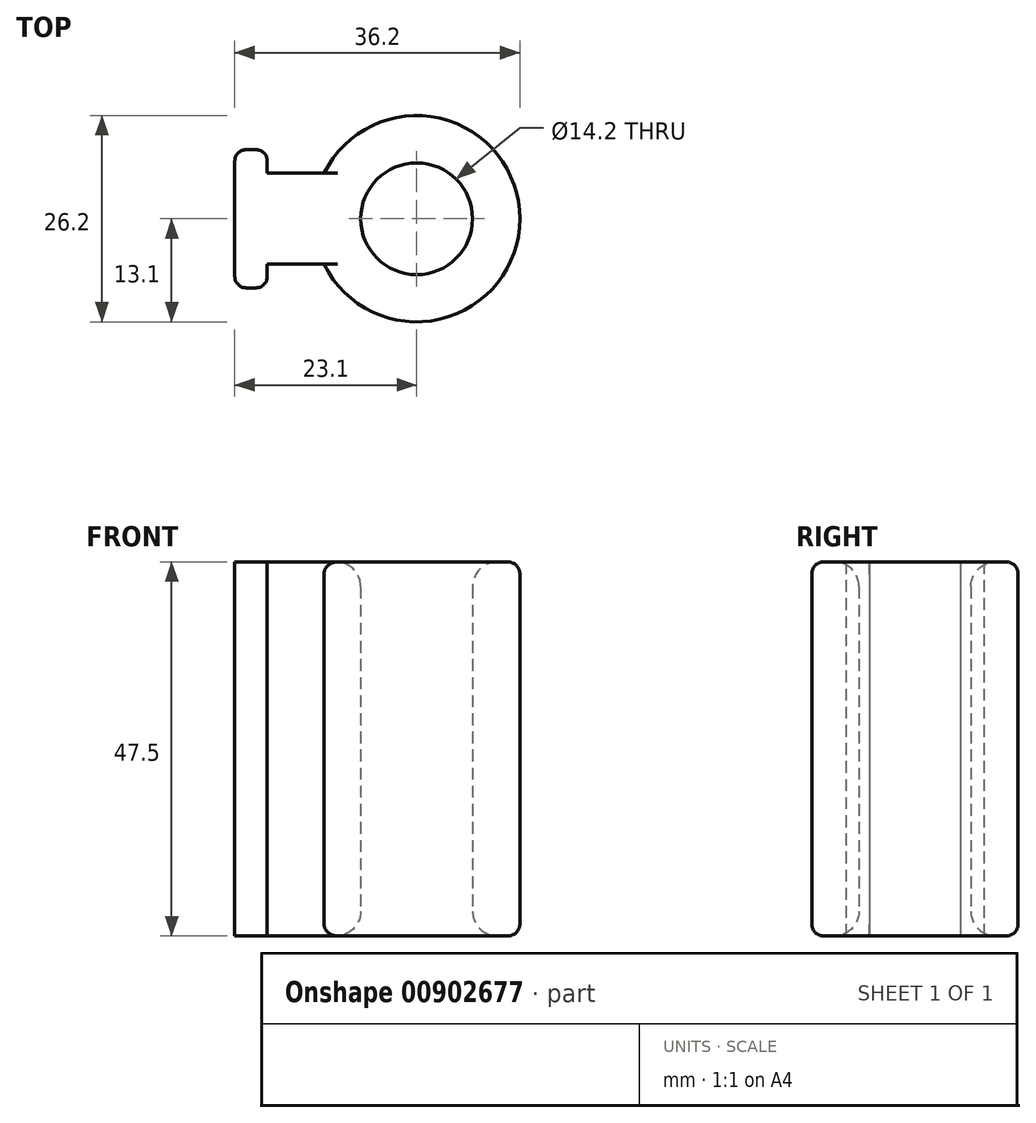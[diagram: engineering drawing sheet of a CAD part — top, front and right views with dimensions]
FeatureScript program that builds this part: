
annotation { "Feature Type Name" : "Feature", "Feature Type Description" : "" }
export const myFeature = defineFeature(function(context is Context, id is Id, definition is map)
    precondition{}
    {
        {
            var Q0;
            Q0=qCreatedBy(makeId("Top.planeOp"),FACE);
            var sketch = newSketch(context, id + "F0", { "sketchPlane" : qUnion([Q0])});
            skCircle(sketch, "E0", {"center": v(0, 0) * mm, "radius": 7.1 * mm});
            skCircle(sketch, "E1", {"center": v(0, 0) * mm, "radius": 13.1 * mm});
            skLineSegment(sketch, "E2.bottom", {"start": v(-11.76, 5.78) * mm, "end": v(-23.1, 5.78) * mm});
            skLineSegment(sketch, "E2.top", {"start": v(-11.76, -5.78) * mm, "end": v(-23.1, -5.78) * mm});
            skLineSegment(sketch, "E2.left", {"start": v(-11.76, 5.78) * mm, "end": v(-11.76, -5.78) * mm});
            skLineSegment(sketch, "E2.right", {"start": v(-23.1, 5.78) * mm, "end": v(-23.1, -5.78) * mm});
            skLineSegment(sketch, "E3.bottom", {"start": v(-23.1, 8.78) * mm, "end": v(-18.97, 8.78) * mm});
            skLineSegment(sketch, "E3.top", {"start": v(-23.1, -8.78) * mm, "end": v(-18.97, -8.78) * mm});
            skLineSegment(sketch, "E3.left", {"start": v(-23.1, 8.78) * mm, "end": v(-23.1, -8.78) * mm});
            skLineSegment(sketch, "E3.right", {"start": v(-18.97, 8.78) * mm, "end": v(-18.97, -8.78) * mm});
            skSolve(sketch);
        }
        {
            var Q0;
            Q0=makeQuery(id+"F0.imprint","IMPRINT",FACE,{"disambiguationData":[TD([[makeQuery(id+"F0.imprint","IMPRINT",EDGE,{"derivedFrom":sQuery(id+"F0.wireOp",EDGE,"E0")}),-1.0]])]});
            var Q1;
            {var subQ1=sQuery(id+"F0.wireOp",EDGE,"E2.bottom");Q1=makeQuery(id+"F0.imprint","IMPRINT",FACE,{"disambiguationData":[TD([[makeQuery(id+"F0.imprint","IMPRINT",EDGE,{"derivedFrom":subQ1}),1.0]])]});}
            var Q2;
            {var subQ0=sQuery(id+"F0.wireOp",EDGE,"E2.left");Q2=makeQuery(id+"F0.imprint","IMPRINT",FACE,{"disambiguationData":[TD([[makeQuery(id+"F0.imprint","IMPRINT",EDGE,{"derivedFrom":subQ0}),-1.0]])]});}
            var Q3;
            {var subQ5=sQuery(id+"F0.wireOp",EDGE,"E3.bottom");Q3=makeQuery(id+"F0.imprint","IMPRINT",FACE,{"disambiguationData":[TD([[makeQuery(id+"F0.imprint","IMPRINT",EDGE,{"derivedFrom":subQ5}),-1.0]])]});}
            var Q4;
            {var subQ5=sQuery(id+"F0.wireOp",EDGE,"E3.top");Q4=makeQuery(id+"F0.imprint","IMPRINT",FACE,{"disambiguationData":[TD([[makeQuery(id+"F0.imprint","IMPRINT",EDGE,{"derivedFrom":subQ5}),1.0]])]});}
            extrude(context, id + "F1", {"entities" : qUnion([Q0, Q1, Q2, Q3, Q4]), "depth" : 47.5 * mm, "offsetDistance" : 25 * mm});
        }
        {
            var Q0;
            Q0=makeQuery(id+"F1.opExtrude","SWEPT_EDGE",EDGE,{"disambiguationData":[OSD([sQuery(id+"F0.wireOp",EDGE,"E3.top"),sQuery(id+"F0.wireOp",EDGE,"E3.left")])]});
            var Q1;
            Q1=makeQuery(id+"F1.opExtrude","SWEPT_EDGE",EDGE,{"disambiguationData":[OSD([sQuery(id+"F0.wireOp",EDGE,"E3.bottom"),sQuery(id+"F0.wireOp",EDGE,"E3.left")])]});
            var Q2;
            Q2=makeQuery(id+"F1.opExtrude","SWEPT_EDGE",EDGE,{"disambiguationData":[OSD([sQuery(id+"F0.wireOp",EDGE,"E3.top"),sQuery(id+"F0.wireOp",EDGE,"E3.right")])]});
            var Q3;
            Q3=makeQuery(id+"F1.opExtrude","SWEPT_EDGE",EDGE,{"disambiguationData":[OSD([sQuery(id+"F0.wireOp",EDGE,"E3.bottom"),sQuery(id+"F0.wireOp",EDGE,"E3.right")])]});
            fillet(context, id + "F2", {"entities" : qUnion([Q0, Q1, Q2, Q3]), "radius" : 1.45 * mm, "tangentPropagation" : true, "allowEdgeOverflow" : false});
        }
        {
            var Q0;
            Q0=makeQuery(id+"F1.opExtrude","CAP_EDGE",EDGE,{"disambiguationData":[OSD([sQuery(id+"F0.wireOp",EDGE,"E0")])],"isStart":false});
            var Q1;
            Q1=makeQuery(id+"F1.opExtrude","CAP_EDGE",EDGE,{"disambiguationData":[OSD([sQuery(id+"F0.wireOp",EDGE,"E0")])],"isStart":true});
            fillet(context, id + "F3", {"entities" : qUnion([Q0, Q1]), "radius" : 3.14 * mm, "tangentPropagation" : true, "allowEdgeOverflow" : false});
        }
        {
            var Q0;
            Q0=makeQuery(id+"F1.opExtrude","CAP_EDGE",EDGE,{"disambiguationData":[OSD([sQuery(id+"F0.wireOp",EDGE,"E1")])],"isStart":false});
            var Q1;
            Q1=makeQuery(id+"F1.opExtrude","CAP_EDGE",EDGE,{"disambiguationData":[OSD([sQuery(id+"F0.wireOp",EDGE,"E1")])],"isStart":true});
            fillet(context, id + "F4", {"entities" : qUnion([Q0, Q1]), "radius" : 1.5 * mm, "tangentPropagation" : true, "allowEdgeOverflow" : false});
        }
    });
